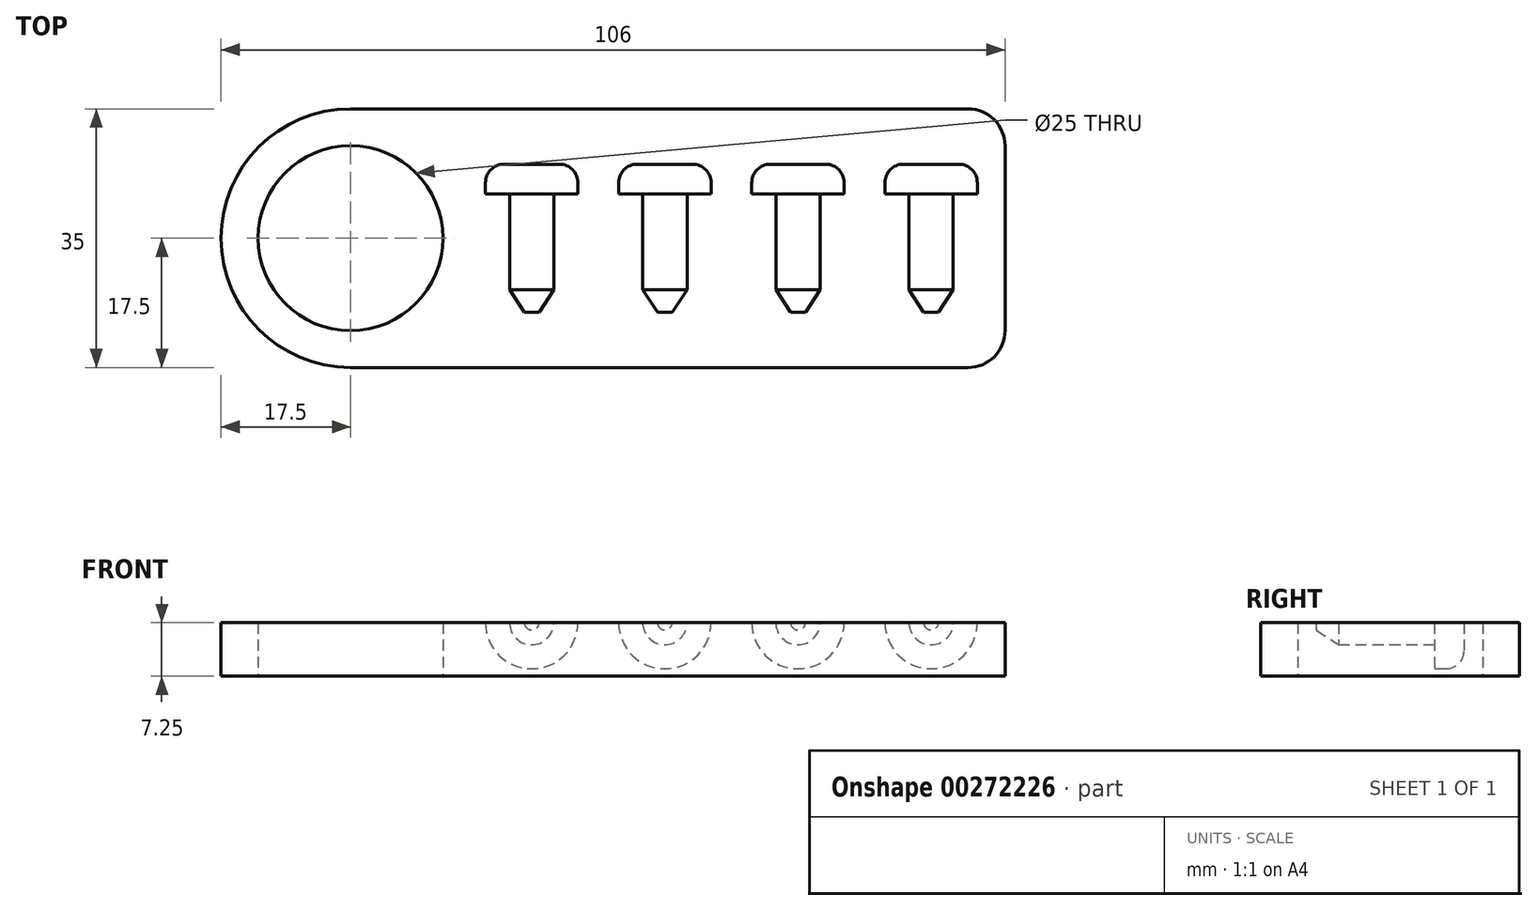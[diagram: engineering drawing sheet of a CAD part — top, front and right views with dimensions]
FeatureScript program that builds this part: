
annotation { "Feature Type Name" : "Feature", "Feature Type Description" : "" }
export const myFeature = defineFeature(function(context is Context, id is Id, definition is map)
    precondition{}
    {
        {
            var Q0;
            Q0=qCreatedBy(makeId("Top.planeOp"),FACE);
            var sketch = newSketch(context, id + "F0", { "sketchPlane" : qUnion([Q0])});
            skLineSegment(sketch, "E0.bottom", {"start": v(17.5, 0) * mm, "end": v(101, 0) * mm});
            skLineSegment(sketch, "E0.top", {"start": v(17.5, 35) * mm, "end": v(101, 35) * mm});
            skLineSegment(sketch, "E0.left", {"start": v(0, 17.5) * mm, "end": v(0, 17.5) * mm});
            skLineSegment(sketch, "E0.right", {"start": v(106, 5) * mm, "end": v(106, 30) * mm});
            skLineSegment(sketch, "E1.bottom", {"start": v(0, 0) * mm, "end": v(17.5, 0) * mm, "construction": true});
            skLineSegment(sketch, "E1.top", {"start": v(0, 17.5) * mm, "end": v(17.5, 17.5) * mm, "construction": true});
            skLineSegment(sketch, "E1.left", {"start": v(0, 0) * mm, "end": v(0, 17.5) * mm, "construction": true});
            skLineSegment(sketch, "E1.right", {"start": v(17.5, 0) * mm, "end": v(17.5, 17.5) * mm, "construction": true});
            skCircle(sketch, "E2", {"center": v(17.5, 17.5) * mm, "radius": 12.5 * mm});
            skPoint(sketch, "E3.visualSharp", {"position": v(0, 0) * mm});
            skArc(sketch, "E3.filletArc", {"start": v(0, 17.5) * mm, "mid": v(5.13, 5.13) * mm, "end": v(17.5, 0) * mm});
            skPoint(sketch, "E4.visualSharp", {"position": v(0, 35) * mm});
            skArc(sketch, "E4.filletArc", {"start": v(17.5, 35) * mm, "mid": v(5.13, 29.87) * mm, "end": v(0, 17.5) * mm});
            skPoint(sketch, "E5.visualSharp", {"position": v(106, 35) * mm});
            skArc(sketch, "E5.filletArc", {"start": v(106, 30) * mm, "mid": v(104.54, 33.54) * mm, "end": v(101, 35) * mm});
            skPoint(sketch, "E6.visualSharp", {"position": v(106, 0) * mm});
            skArc(sketch, "E6.filletArc", {"start": v(101, 0) * mm, "mid": v(104.54, 1.46) * mm, "end": v(106, 5) * mm});
            skSolve(sketch);
        }
        {
            var Q0;
            Q0=makeQuery(id+"F0.imprint","IMPRINT",FACE,{"disambiguationData":[TD([[makeQuery(id+"F0.imprint","IMPRINT",EDGE,{"derivedFrom":sQuery(id+"F0.wireOp",EDGE,"E0.bottom")}),1.0]])]});
            extrude(context, id + "F1", {"entities" : qUnion([Q0]), "depth" : 7.25 * mm});
        }
        {
            var Q0;
            Q0=makeQuery(id+"F1.opExtrude","CAP_FACE",FACE,{"disambiguationData":[OSD([sQuery(id+"F0.wireOp",EDGE,"E0.bottom"),sQuery(id+"F0.wireOp",EDGE,"E0.top"),sQuery(id+"F0.wireOp",EDGE,"E0.right"),sQuery(id+"F0.wireOp",EDGE,"E2"),sQuery(id+"F0.wireOp",EDGE,"E3.filletArc"),sQuery(id+"F0.wireOp",EDGE,"E4.filletArc"),sQuery(id+"F0.wireOp",EDGE,"E5.filletArc"),sQuery(id+"F0.wireOp",EDGE,"E6.filletArc")])],"isStart":false});
            var sketch = newSketch(context, id + "F2", { "sketchPlane" : qUnion([Q0])});
            skLineSegment(sketch, "E7.bottom", {"start": v(0, 0) * mm, "end": v(42, 0) * mm, "construction": true});
            skLineSegment(sketch, "E7.top", {"start": v(0, 7.5) * mm, "end": v(42, 7.5) * mm, "construction": true});
            skLineSegment(sketch, "E7.left", {"start": v(0, 0) * mm, "end": v(0, 7.5) * mm, "construction": true});
            skLineSegment(sketch, "E7.right", {"start": v(42, 0) * mm, "end": v(42, 7.5) * mm, "construction": true});
            skLineSegment(sketch, "E8", {"start": v(42, 7.5) * mm, "end": v(60, 7.5) * mm, "construction": true});
            skLineSegment(sketch, "E9", {"start": v(42, 7.5) * mm, "end": v(42, 23.5) * mm});
            skLineSegment(sketch, "E10", {"start": v(60, 7.5) * mm, "end": v(60, 23.5) * mm});
            skLineSegment(sketch, "E11", {"start": v(60, 7.5) * mm, "end": v(61, 7.5) * mm});
            skLineSegment(sketch, "E12", {"start": v(42, 7.5) * mm, "end": v(43, 7.5) * mm});
            skLineSegment(sketch, "E13.bottom", {"start": v(42, 27.5) * mm, "end": v(45.75, 27.5) * mm});
            skLineSegment(sketch, "E13.top", {"start": v(45, 23.5) * mm, "end": v(48.25, 23.5) * mm});
            skLineSegment(sketch, "E13.left", {"start": v(42, 27.5) * mm, "end": v(42, 23.5) * mm});
            skLineSegment(sketch, "E13.right", {"start": v(48.25, 25) * mm, "end": v(48.25, 23.5) * mm});
            skLineSegment(sketch, "E14.bottom", {"start": v(60, 27.5) * mm, "end": v(63.75, 27.5) * mm});
            skLineSegment(sketch, "E14.top", {"start": v(63, 23.5) * mm, "end": v(66.25, 23.5) * mm});
            skLineSegment(sketch, "E14.left", {"start": v(60, 27.5) * mm, "end": v(60, 23.5) * mm});
            skLineSegment(sketch, "E14.right", {"start": v(66.25, 25) * mm, "end": v(66.25, 23.5) * mm});
            skLineSegment(sketch, "E15.left", {"start": v(42, 23.5) * mm, "end": v(42, 10.5) * mm});
            skLineSegment(sketch, "E15.right", {"start": v(45, 23.5) * mm, "end": v(45, 10.5) * mm});
            skLineSegment(sketch, "E16.left", {"start": v(60, 23.5) * mm, "end": v(60, 10.5) * mm});
            skLineSegment(sketch, "E16.right", {"start": v(63, 23.5) * mm, "end": v(63, 10.5) * mm});
            skLineSegment(sketch, "E17", {"start": v(43, 7.5) * mm, "end": v(45, 10.5) * mm});
            skLineSegment(sketch, "E18", {"start": v(61, 7.5) * mm, "end": v(63, 10.5) * mm});
            skPoint(sketch, "E19.visualSharp", {"position": v(48.25, 27.5) * mm});
            skArc(sketch, "E19.filletArc", {"start": v(48.25, 25) * mm, "mid": v(47.52, 26.77) * mm, "end": v(45.75, 27.5) * mm});
            skPoint(sketch, "E20.visualSharp", {"position": v(66.25, 27.5) * mm});
            skArc(sketch, "E20.filletArc", {"start": v(66.25, 25) * mm, "mid": v(65.52, 26.77) * mm, "end": v(63.75, 27.5) * mm});
            skLineSegment(sketch, "E21", {"start": v(60, 7.5) * mm, "end": v(78, 7.5) * mm, "construction": true});
            skLineSegment(sketch, "E22", {"start": v(78, 7.5) * mm, "end": v(96, 7.5) * mm, "construction": true});
            skLineSegment(sketch, "E23", {"start": v(96, 7.5) * mm, "end": v(97, 7.5) * mm});
            skLineSegment(sketch, "E24", {"start": v(78, 7.5) * mm, "end": v(79, 7.5) * mm});
            skLineSegment(sketch, "E25", {"start": v(78, 7.5) * mm, "end": v(78, 27.5) * mm});
            skLineSegment(sketch, "E26", {"start": v(96, 7.5) * mm, "end": v(96, 23.5) * mm});
            skLineSegment(sketch, "E27.bottom", {"start": v(78, 27.5) * mm, "end": v(81.75, 27.5) * mm});
            skLineSegment(sketch, "E27.top", {"start": v(81, 23.5) * mm, "end": v(84.25, 23.5) * mm});
            skLineSegment(sketch, "E27.right", {"start": v(84.25, 25) * mm, "end": v(84.25, 23.5) * mm});
            skLineSegment(sketch, "E28.bottom", {"start": v(96, 27.5) * mm, "end": v(99.75, 27.5) * mm});
            skLineSegment(sketch, "E28.top", {"start": v(99, 23.5) * mm, "end": v(102.25, 23.5) * mm});
            skLineSegment(sketch, "E28.left", {"start": v(96, 27.5) * mm, "end": v(96, 23.5) * mm});
            skLineSegment(sketch, "E28.right", {"start": v(102.25, 25) * mm, "end": v(102.25, 23.5) * mm});
            skLineSegment(sketch, "E29.left", {"start": v(78, 23.5) * mm, "end": v(78, 10.5) * mm});
            skLineSegment(sketch, "E29.right", {"start": v(81, 23.5) * mm, "end": v(81, 10.5) * mm});
            skLineSegment(sketch, "E30.left", {"start": v(96, 23.5) * mm, "end": v(96, 10.5) * mm});
            skLineSegment(sketch, "E30.right", {"start": v(99, 23.5) * mm, "end": v(99, 10.5) * mm});
            skLineSegment(sketch, "E31", {"start": v(99, 10.5) * mm, "end": v(97, 7.5) * mm});
            skLineSegment(sketch, "E32", {"start": v(81, 10.5) * mm, "end": v(79, 7.5) * mm});
            skPoint(sketch, "E33.visualSharp", {"position": v(84.25, 27.5) * mm});
            skArc(sketch, "E33.filletArc", {"start": v(84.25, 25) * mm, "mid": v(83.52, 26.77) * mm, "end": v(81.75, 27.5) * mm});
            skPoint(sketch, "E34.visualSharp", {"position": v(102.25, 27.5) * mm});
            skArc(sketch, "E34.filletArc", {"start": v(102.25, 25) * mm, "mid": v(101.52, 26.77) * mm, "end": v(99.75, 27.5) * mm});
            skSolve(sketch);
        }
        {
            var Q0;
            Q0=makeQuery(id+"F2.imprint","IMPRINT",FACE,{"disambiguationData":[TD([[makeQuery(id+"F2.imprint","IMPRINT",EDGE,{"derivedFrom":sQuery(id+"F2.wireOp",EDGE,"E9")}),-1.0]])]});
            var Q1;
            Q1=sQuery(id+"F2.wireOp",EDGE,"E9");
            revolve(context, id + "F3", {"operationType" : NewBodyOperationType.REMOVE, "entities" : qUnion([Q0]), "axis" : qUnion([Q1]), "revolveType" : RevolveType.FULL, "oppositeDirection" : true});
        }
        {
            var Q0;
            Q0=makeQuery(id+"F2.imprint","IMPRINT",FACE,{"disambiguationData":[TD([[makeQuery(id+"F2.imprint","IMPRINT",EDGE,{"derivedFrom":sQuery(id+"F2.wireOp",EDGE,"E10")}),-1.0]])]});
            var Q1;
            Q1=sQuery(id+"F2.wireOp",EDGE,"E10");
            revolve(context, id + "F4", {"operationType" : NewBodyOperationType.REMOVE, "entities" : qUnion([Q0]), "axis" : qUnion([Q1]), "revolveType" : RevolveType.FULL, "oppositeDirection" : true});
        }
        {
            var Q0;
            {var subQ2=sQuery(id+"F2.wireOp",EDGE,"E24");Q0=makeQuery(id+"F2.imprint","IMPRINT",FACE,{"disambiguationData":[TD([[makeQuery(id+"F2.imprint","IMPRINT",EDGE,{"derivedFrom":subQ2}),1.0]])]});}
            var Q1;
            Q1=sQuery(id+"F2.wireOp",EDGE,"E29.left");
            revolve(context, id + "F5", {"operationType" : NewBodyOperationType.REMOVE, "entities" : qUnion([Q0]), "axis" : qUnion([Q1]), "revolveType" : RevolveType.FULL, "oppositeDirection" : true});
        }
        {
            var Q0;
            Q0=makeQuery(id+"F2.imprint","IMPRINT",FACE,{"disambiguationData":[TD([[makeQuery(id+"F2.imprint","IMPRINT",EDGE,{"derivedFrom":sQuery(id+"F2.wireOp",EDGE,"E23")}),1.0]])]});
            var Q1;
            Q1=sQuery(id+"F2.wireOp",EDGE,"E26");
            revolve(context, id + "F6", {"operationType" : NewBodyOperationType.REMOVE, "entities" : qUnion([Q0]), "axis" : qUnion([Q1]), "revolveType" : RevolveType.FULL, "oppositeDirection" : true});
        }
    });
